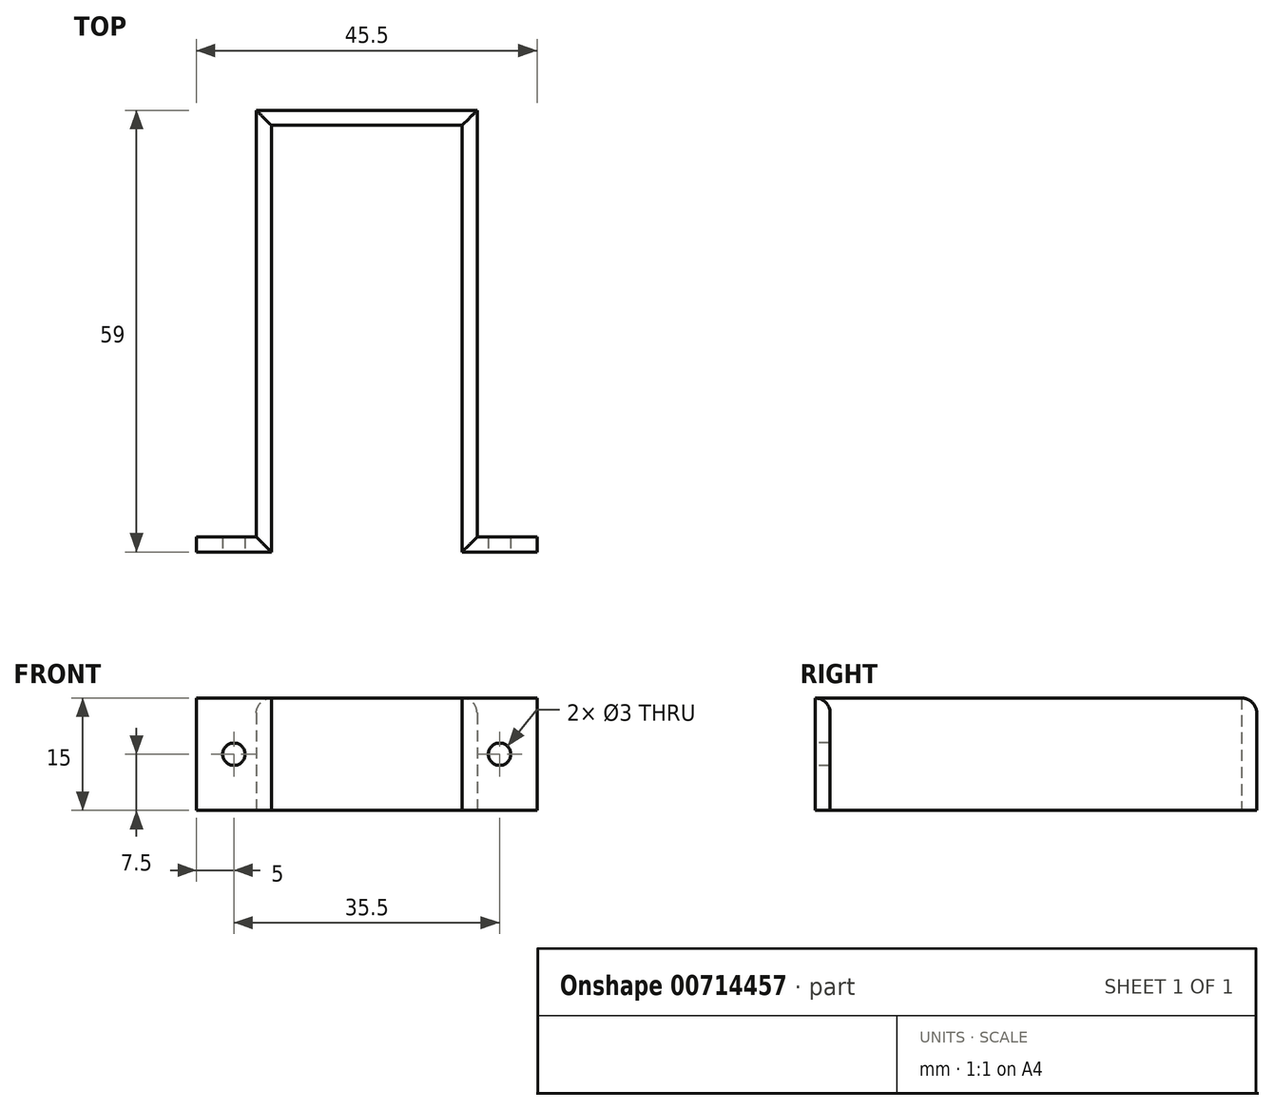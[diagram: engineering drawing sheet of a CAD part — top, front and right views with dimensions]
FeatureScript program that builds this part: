
annotation { "Feature Type Name" : "Feature", "Feature Type Description" : "" }
export const myFeature = defineFeature(function(context is Context, id is Id, definition is map)
    precondition{}
    {
        {
            var Q0;
            Q0=qCreatedBy(makeId("Top.planeOp"),FACE);
            var sketch = newSketch(context, id + "F0", { "sketchPlane" : qUnion([Q0])});
            skLineSegment(sketch, "E0", {"start": v(-22.75, 0) * mm, "end": v(-12.75, 0) * mm});
            skLineSegment(sketch, "E1", {"start": v(-12.75, 0) * mm, "end": v(-12.75, 57) * mm});
            skLineSegment(sketch, "E2", {"start": v(-12.75, 57) * mm, "end": v(0, 57) * mm});
            skLineSegment(sketch, "E3.MirrorCS", {"start": v(12.75, 57) * mm, "end": v(0, 57) * mm});
            skLineSegment(sketch, "E4.MirrorCS", {"start": v(12.75, 0) * mm, "end": v(12.75, 57) * mm});
            skLineSegment(sketch, "E5.MirrorCS", {"start": v(22.75, 0) * mm, "end": v(12.75, 0) * mm});
            skLineSegment(sketch, "E6.0", {"start": v(22.75, 2) * mm, "end": v(14.75, 2) * mm});
            skLineSegment(sketch, "E6.1", {"start": v(14.75, 2) * mm, "end": v(14.75, 59) * mm});
            skLineSegment(sketch, "E6.2", {"start": v(-22.75, 2) * mm, "end": v(-14.75, 2) * mm});
            skLineSegment(sketch, "E6.3", {"start": v(-14.75, 2) * mm, "end": v(-14.75, 59) * mm});
            skLineSegment(sketch, "E6.4", {"start": v(-14.75, 59) * mm, "end": v(0, 59) * mm});
            skLineSegment(sketch, "E6.5", {"start": v(14.75, 59) * mm, "end": v(0, 59) * mm});
            skLineSegment(sketch, "E7", {"start": v(-22.75, 2) * mm, "end": v(-22.75, 0) * mm});
            skLineSegment(sketch, "E8", {"start": v(22.75, 2) * mm, "end": v(22.75, 0) * mm});
            skSolve(sketch);
        }
        {
            var Q0;
            Q0 = qSketchRegion(id + "F0", true);
            extrude(context, id + "F1", {"entities" : qUnion([Q0]), "depth" : 15 * mm, "offsetDistance" : 25 * mm});
        }
        {
            var Q0;
            Q0=qCreatedBy(makeId("Front.planeOp"),FACE);
            var sketch = newSketch(context, id + "F2", { "sketchPlane" : qUnion([Q0])});
            skCircle(sketch, "E9", {"center": v(-17.75, 7.5) * mm, "radius": 1.5 * mm});
            skCircle(sketch, "E10.MirrorC", {"center": v(17.75, 7.5) * mm, "radius": 1.5 * mm});
            skSolve(sketch);
        }
        {
            var Q0;
            Q0 = qSketchRegion(id + "F2", true);
            extrude(context, id + "F3", {"entities" : qUnion([Q0]), "operationType" : NewBodyOperationType.REMOVE, "oppositeDirection" : true, "depth" : 2 * mm, "offsetDistance" : 25 * mm});
        }
        {
            var Q0;
            Q0=makeQuery(id+"F1.opExtrude","CAP_EDGE",EDGE,{"disambiguationData":[OSD([sQuery(id+"F0.wireOp",EDGE,"E6.3")])],"isStart":false});
            var Q1;
            Q1=makeQuery(id+"F1.opExtrude","CAP_EDGE",EDGE,{"disambiguationData":[OSD([sQuery(id+"F0.wireOp",EDGE,"E6.4"),sQuery(id+"F0.wireOp",EDGE,"E6.5")])],"isStart":false});
            var Q2;
            Q2=makeQuery(id+"F1.opExtrude","CAP_EDGE",EDGE,{"disambiguationData":[OSD([sQuery(id+"F0.wireOp",EDGE,"E6.1")])],"isStart":false});
            var Q3;
            Q3=makeQuery(id+"F1.opExtrude","CAP_EDGE",EDGE,{"disambiguationData":[OSD([sQuery(id+"F0.wireOp",EDGE,"E6.0")])],"isStart":false});
            var Q4;
            Q4=makeQuery(id+"F1.opExtrude","CAP_EDGE",EDGE,{"disambiguationData":[OSD([sQuery(id+"F0.wireOp",EDGE,"E6.2")])],"isStart":false});
            fillet(context, id + "F4", {"entities" : qUnion([Q0, Q1, Q2, Q3, Q4]), "radius" : 2 * mm, "tangentPropagation" : true, "allowEdgeOverflow" : false});
        }
    });
